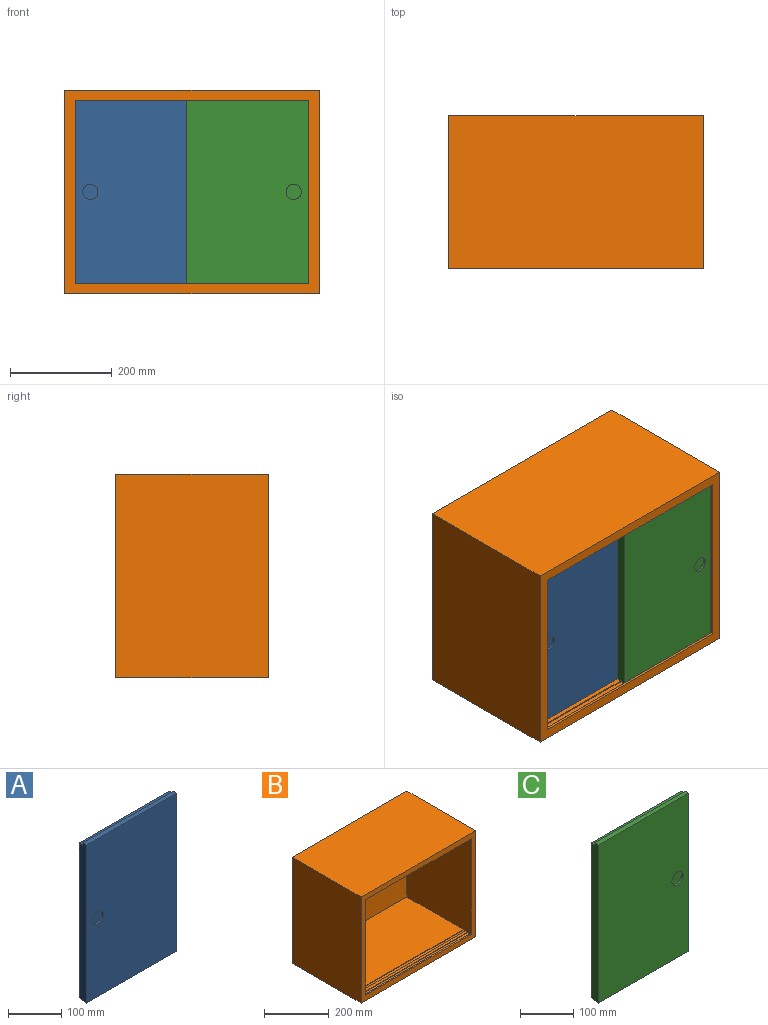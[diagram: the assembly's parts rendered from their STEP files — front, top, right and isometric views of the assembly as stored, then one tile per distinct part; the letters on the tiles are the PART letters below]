
ASSEMBLY  parts=3 mates=2
PART A: 12 faces, bbox 240x20x364.5 mm
  f0: plane 240x5mm, normal (0,1,0), area 1200mm2, adj f2,f3,f8,f9
  f1: plane 364.5x240mm, normal (0,-1,0), area 86773.1mm2, adj f2,f3,f5,f8,f10
  f2: plane 364.5x20mm, normal (1,0,0), area 7220mm2, adj f0,f1,f4,f5,f6,f7,f8,f9
  f3: plane 364.5x20mm, normal (-1,0,0), area 7220mm2, adj f0,f1,f4,f5,f6,f7,f8,f9
  f4: plane 357.5x240mm, normal (0,1,0), area 85800mm2, adj f2,f3,f7,f9
  f5: plane 240x10mm, normal (0,0,-1), area 2400mm2, adj f1,f2,f3,f6
  f6: plane 240x2mm, normal (0,1,0), area 480mm2, adj f2,f3,f5,f7
  f7: plane 240x10mm, normal (0,0,-1), area 2400mm2, adj f2,f3,f4,f6
  f8: plane 240x10mm, normal (0,0,1), area 2400mm2, adj f0,f1,f2,f3
  f9: plane 240x10mm, normal (0,0,1), area 2400mm2, adj f0,f2,f3,f4
  f10: cylinder r=15mm len=30mm, axis (0,-1,0), area 471.2mm2, adj f1,f11
  f11: plane 30x30mm, normal (0,-1,0), area 706.9mm2, adj f10
PART B: 27 faces, bbox 500x300x400 mm
  f0: plane 460x10mm, normal (0,0,-1), area 4600mm2, adj f10,f12,f21,f24
  f1: plane 460x245mm, normal (0,0,-1), area 112700mm2, adj f10,f11,f12,f22
  f2: plane 460x10mm, normal (0,0,1), area 4600mm2, adj f10,f12,f17,f19
  f3: plane 460x245mm, normal (0,0,1), area 112700mm2, adj f10,f11,f12,f16
  f4: plane 500x400mm, normal (0,-1,0), area 34400mm2, adj f5,f7,f8,f9,f10,f12,f13,f14
  f5: plane 400x300mm, normal (1,0,0), area 120000mm2, adj f4,f6,f8,f9
  f6: plane 500x400mm, normal (0,1,0), area 200000mm2, adj f5,f7,f8,f9
  f7: plane 400x300mm, normal (-1,0,0), area 120000mm2, adj f4,f6,f8,f9
  f8: plane 500x300mm, normal (0,0,1), area 150000mm2, adj f4,f5,f6,f7
  f9: plane 500x300mm, normal (0,0,-1), area 150000mm2, adj f4,f5,f6,f7
  f10: plane 367x280mm, normal (-1,0,0), area 100940mm2, adj f0,f1,f2,f3,f4,f11,f13,f14
  f11: plane 460x360mm, normal (0,-1,0), area 165600mm2, adj f1,f3,f10,f12
  f12: plane 367x280mm, normal (1,0,0), area 100940mm2, adj f0,f1,f2,f3,f4,f11,f13,f14
  f13: plane 460x5mm, normal (0,0,-1), area 2300mm2, adj f4,f10,f12,f25
  f14: plane 460x5mm, normal (0,0,1), area 2300mm2, adj f4,f10,f12,f20
  f15: plane 460x10mm, normal (0,0,1), area 4600mm2, adj f10,f12,f16,f17
  f16: plane 460x2mm, normal (0,-1,0), area 920mm2, adj f3,f10,f12,f15
  f17: plane 460x2mm, normal (0,1,0), area 920mm2, adj f2,f10,f12,f15
  f18: plane 460x10mm, normal (0,0,1), area 4600mm2, adj f10,f12,f19,f20
  f19: plane 460x2mm, normal (0,-1,0), area 920mm2, adj f2,f10,f12,f18
  f20: plane 460x2mm, normal (0,1,0), area 920mm2, adj f10,f12,f14,f18
  f21: plane 460x5mm, normal (0,1,0), area 2300mm2, adj f0,f10,f12,f23
  f22: plane 460x5mm, normal (0,-1,0), area 2300mm2, adj f1,f10,f12,f23
  f23: plane 460x10mm, normal (0,0,-1), area 4600mm2, adj f10,f12,f21,f22
  f24: plane 460x5mm, normal (0,-1,0), area 2300mm2, adj f0,f10,f12,f26
  f25: plane 460x5mm, normal (0,1,0), area 2300mm2, adj f10,f12,f13,f26
  f26: plane 460x10mm, normal (0,0,-1), area 4600mm2, adj f10,f12,f24,f25
PART C: 12 faces, bbox 240x20x364.5 mm
  f0: plane 364.5x240mm, normal (0,-1,0), area 86773.1mm2, adj f3,f4,f7,f8,f10
  f1: plane 357.5x240mm, normal (0,1,0), area 85800mm2, adj f3,f6,f7,f9
  f2: plane 240x5mm, normal (0,1,0), area 1200mm2, adj f3,f7,f8,f9
  f3: plane 364.5x20mm, normal (-1,0,0), area 7220mm2, adj f0,f1,f2,f4,f5,f6,f8,f9
  f4: plane 240x10mm, normal (0,0,-1), area 2400mm2, adj f0,f3,f5,f7
  f5: plane 240x2mm, normal (0,1,0), area 480mm2, adj f3,f4,f6,f7
  f6: plane 240x10mm, normal (0,0,-1), area 2400mm2, adj f1,f3,f5,f7
  f7: plane 364.5x20mm, normal (1,0,0), area 7220mm2, adj f0,f1,f2,f4,f5,f6,f8,f9
  f8: plane 240x10mm, normal (0,0,1), area 2400mm2, adj f0,f2,f3,f7
  f9: plane 240x10mm, normal (0,0,1), area 2400mm2, adj f1,f2,f3,f7
  f10: cylinder r=15mm len=30mm, axis (0,-1,0), area 471.2mm2, adj f0,f11
  f11: plane 30x30mm, normal (0,-1,0), area 706.9mm2, adj f10
PLACE A at identity
PLACE B at identity fixed
PLACE C at identity
MATE slider B.f10 <-> C.f7  axis (-1,0,0) through (230,-135,20)mm
MATE slider B.f12 <-> A.f3  axis (1,0,0) through (-230,-115,20)mm
